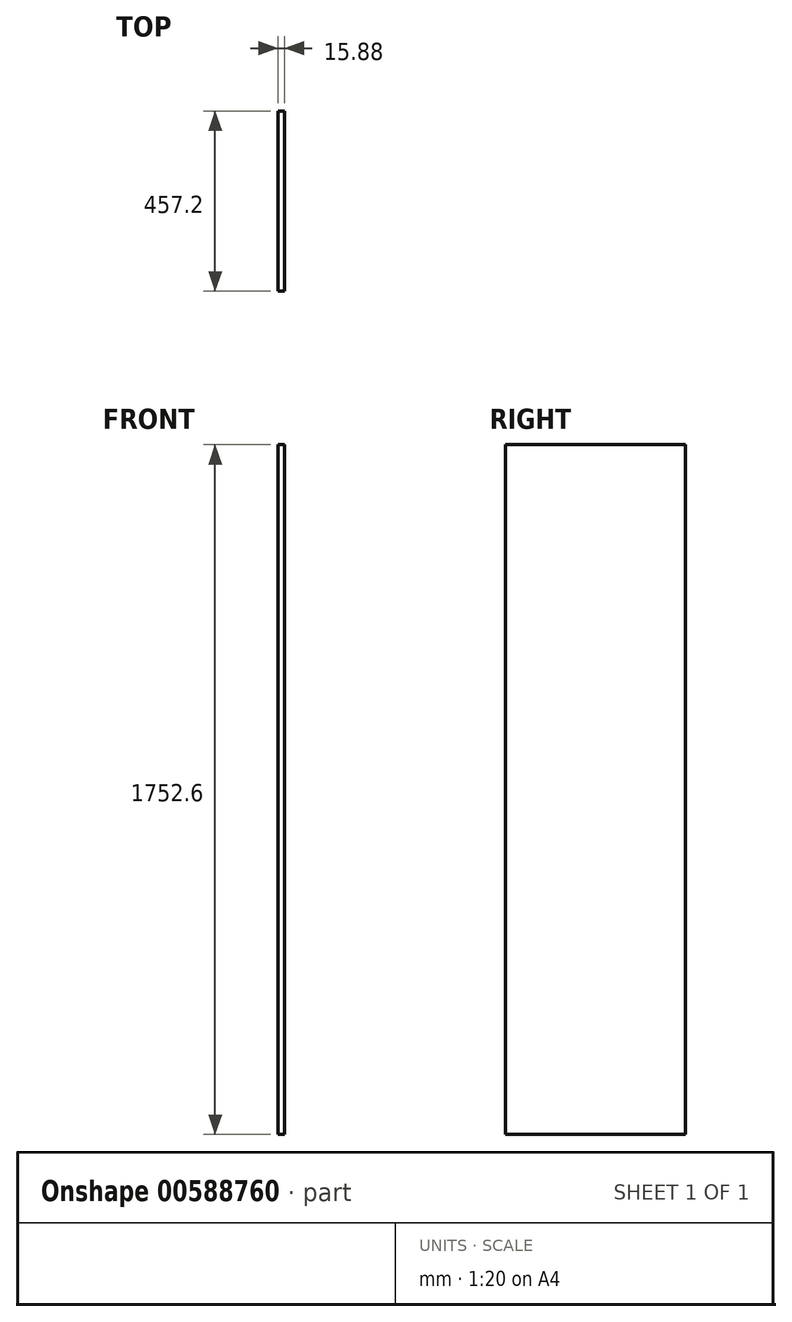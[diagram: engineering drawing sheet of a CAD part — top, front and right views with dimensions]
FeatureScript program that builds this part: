
annotation { "Feature Type Name" : "Feature", "Feature Type Description" : "" }
export const myFeature = defineFeature(function(context is Context, id is Id, definition is map)
    precondition{}
    {
        {
            var Q0;
            Q0=qCreatedBy(makeId("Right.planeOp"),FACE);
            var sketch = newSketch(context, id + "F0", { "sketchPlane" : qUnion([Q0])});
            skLineSegment(sketch, "E0.bottom", {"start": v(0, 0) * mm, "end": v(457.2, 0) * mm});
            skLineSegment(sketch, "E0.top", {"start": v(0, 1752.6) * mm, "end": v(457.2, 1752.6) * mm});
            skLineSegment(sketch, "E0.left", {"start": v(0, 0) * mm, "end": v(0, 1752.6) * mm});
            skLineSegment(sketch, "E0.right", {"start": v(457.2, 0) * mm, "end": v(457.2, 1752.6) * mm});
            skSolve(sketch);
        }
        {
            var Q0;
            Q0=makeQuery(id+"F0.imprint","IMPRINT",FACE,{"disambiguationData":[TD([[makeQuery(id+"F0.imprint","IMPRINT",EDGE,{"derivedFrom":sQuery(id+"F0.wireOp",EDGE,"E0.bottom")}),1.0]])]});
            extrude(context, id + "F1", {"entities" : qUnion([Q0]), "depth" : 15.88 * mm, "offsetDistance" : 25.4 * mm});
        }
    });
